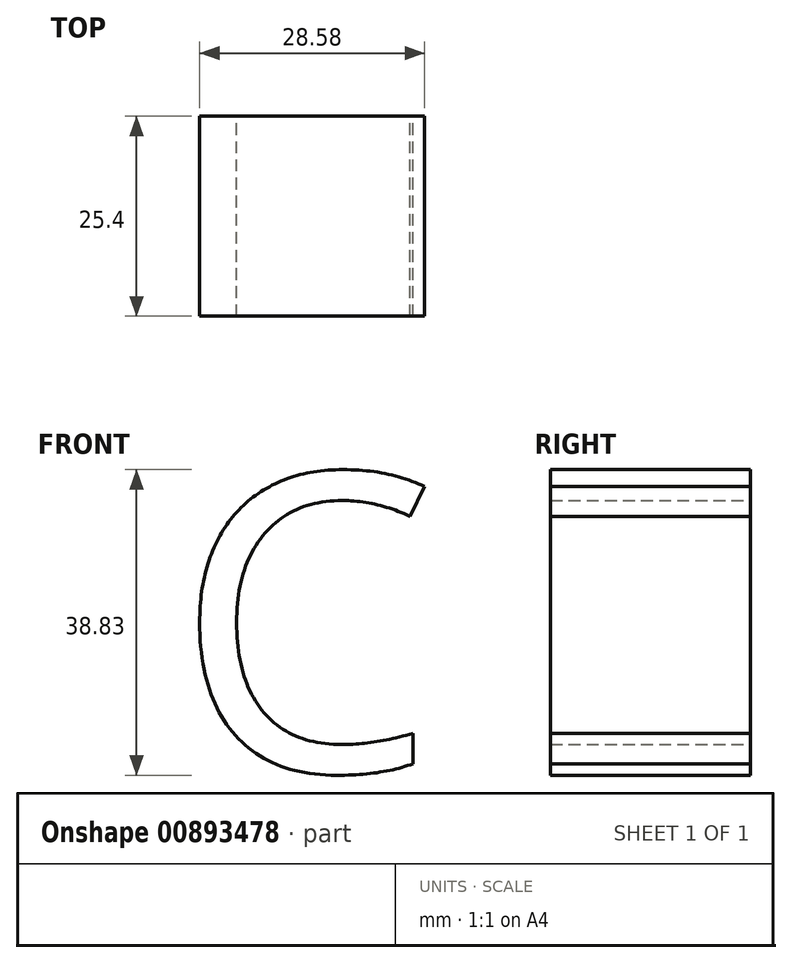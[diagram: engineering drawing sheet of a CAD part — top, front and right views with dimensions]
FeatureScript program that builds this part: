
annotation { "Feature Type Name" : "Feature", "Feature Type Description" : "" }
export const myFeature = defineFeature(function(context is Context, id is Id, definition is map)
    precondition{}
    {
        {
            var Q0;
            Q0=qCreatedBy(makeId("Front.planeOp"),FACE);
            var sketch = newSketch(context, id + "F0", { "sketchPlane" : qUnion([Q0])});
            skText(sketch, "E0", { "text": "C ", "fontName": "OpenSans-Regular.ttf"});
            const initialGuessF0  = {"E0": [-0.01458, -0.0199, 1, 0, 0.0381]};
            skSetInitialGuess(sketch, initialGuessF0);
            skSolve(sketch);
        }
        {
            var Q0;
            Q0 = qSketchRegion(id + "F0", true);
            extrude(context, id + "F1", {"entities" : qUnion([Q0]), "depth" : 25.4 * mm, "offsetDistance" : 25.4 * mm});
        }
    });
